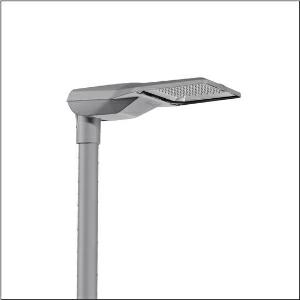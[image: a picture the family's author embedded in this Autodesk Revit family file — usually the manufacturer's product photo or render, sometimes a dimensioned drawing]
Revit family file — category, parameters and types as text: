
# Revit family: streetlight_sl_21_iq_midi___st0_5a_5xe3b31d08mb_db69
name_source: partatom
category: Lighting Fixtures
units: mm (PartAtom-declared; Revit-internal decimal feet)

## family parameters
Cut with Voids When Loaded = No
Host = Face
Light Source = No
Part Type = Normal
Room Calculation Point = No
Round Connector Dimension = Use Diameter
Shared = No

## types (1)
- --- (1 x LED, 19500 lm, 146.7 W, 3000K)
    Apparent Load = 147 VA
    CIE Flux Codes = 41 75 97 100 100
    Color Rendering = 70
    Color Temperature = 3000K
    Default Elevation = 1800 mm
    Description = Streetlight SL 21 iQ midi, mast luminaire, primary light control with lens, of PMMA, primary optical cover: cover, of toughened safety glass, transparent, light distribution: ST0.5a, light emission: direct distribution, primary light characteristic: asymmetric, installation type: post-top, side-entry, LED, High Power LED, rated luminous flux: 19.500lm, luminous efficacy: 133lm/W, light colour: 730, colour temperature: 3000K, control: Auto-Match, Temp-Guard, Lumen-Switch, Night-Set, Smart-Wire, Light-Fading, Desk-Remote (wireless, voltage-free reading and setting of iQ features in the workshop via application-optimized NFC function/RFID function), optimised constant luminous flux control (CLO 2.0), pre-setting: linear dimming characteristic, mains connection: 230..240V, AC, 50/60Hz, start of lifetime: 147W, end of service life: 161W, reduction: 62W, luminaire housing, of diecast aluminium, powder-coated, Siteco® metallic grey (DB 702S), corrosivity category C5 mid according to DIN EN ISO 12944, please order mast flange separately, inclination adjustable: 0°, 5°, 10°, 15°, sealing non-destructively replaceable, multi-level sealing system, length: 644mm, width: 335mm, height: 110mm, mast flange for spigot size: 42mm (side-entry): 5XC10008XM4, 60/48mm (side-entry/post-top): 5XC10108XM2, 76/60mm (side-entry/post-top): 5XC10108XM1, protection rating (complete): IP66, insulation class (complete): insulation class II (safety insulation), certification: CE, ENEC, ENEC+, VDE, impact resistance: IK09, permissible operating ambient temperature for outdoor applications: -40..+50°C, standard-compliant lighting for roads and squares, packaging unit: 1 piece

Light Distribution: ST0.5a
    Height = 111 mm
    Lamp = 1 x LED
    Lamp Light Flux = 19500 lm
    Lamp Power = 146.7 W
    Lamp count = 1
    Length = 644 mm
    Luminous efficacy = 133 lm/W
    Manufacturer = Siteco
    ModVariant = No
    Model = 5XE3B31D08MB
    Number of Poles = 1
    OnlyDefault = Yes
    Power Factor = 1
    Product Name = Streetlight SL 21 iQ midi | ST0.5a
    Product group = mast luminaire | pylon top
    ProductGroupID = 6100
    Protection Class = Protection class II
    Protection Degree = IP 66
    RLX_Detail_Level = 1
    RLX_Emergency_Light_Flux = 0 lm
    RLX_Emergency_Type = 0
    RLX_Emergency_Type_DB = No
    RlxData = <blob elided: 101913 chars, md5=45fa1afa>
    Socket = socket
    Standby Power = 0 W
    System Light Flux = 19499 lm
    System Power = 147 W
    Type Comments = factory setting: luminous flux: 100 % | dim-lin: 254 | 753 mA
    Type Image = l_1004298.jpg
    URL = http://relux.com
    VarID = @adj_164557
    Voltage = 0 V
    Weight = 0.00 kg
    Width = 336 mm

## geometry (parser evidence)
native form markers: Blend x4, Sweep x11
no freeform markers — native parametric forms only
